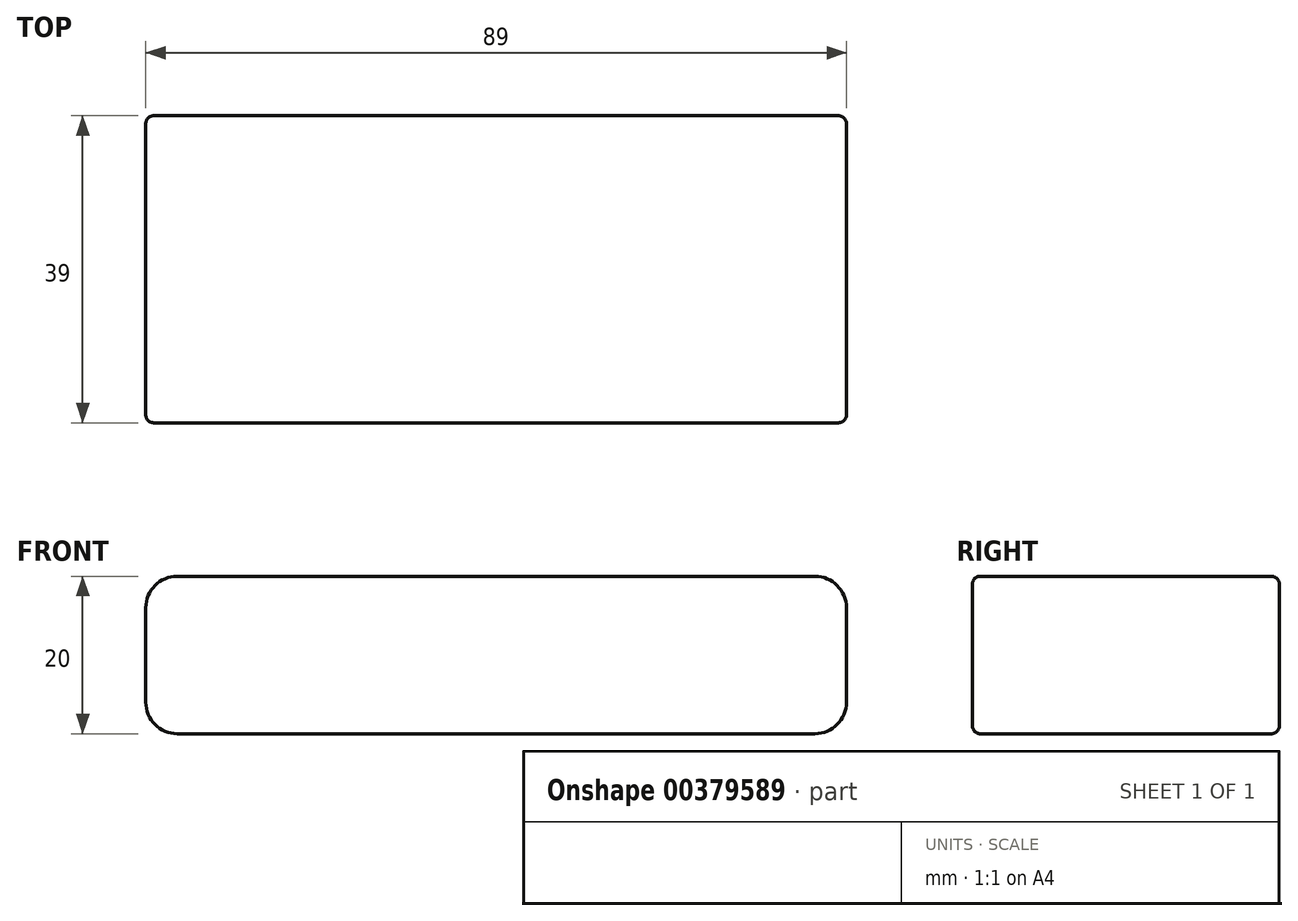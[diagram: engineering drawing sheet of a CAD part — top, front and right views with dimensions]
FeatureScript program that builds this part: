
annotation { "Feature Type Name" : "Feature", "Feature Type Description" : "" }
export const myFeature = defineFeature(function(context is Context, id is Id, definition is map)
    precondition{}
    {
        {
            var Q0;
            Q0=qCreatedBy(makeId("Top.planeOp"),FACE);
            var sketch = newSketch(context, id + "F0", { "sketchPlane" : qUnion([Q0])});
            skLineSegment(sketch, "E0.bottom", {"start": v(44.5, 19.5) * mm, "end": v(-44.5, 19.5) * mm});
            skLineSegment(sketch, "E0.top", {"start": v(44.5, -19.5) * mm, "end": v(-44.5, -19.5) * mm});
            skLineSegment(sketch, "E0.left", {"start": v(44.5, 19.5) * mm, "end": v(44.5, -19.5) * mm});
            skLineSegment(sketch, "E0.right", {"start": v(-44.5, 19.5) * mm, "end": v(-44.5, -19.5) * mm});
            skPoint(sketch, "E0.middle", {"position": v(0, 0) * mm});
            skSolve(sketch);
        }
        {
            var Q0;
            Q0=makeQuery(id+"F0.imprint","IMPRINT",FACE,{"disambiguationData":[TD([[makeQuery(id+"F0.imprint","IMPRINT",EDGE,{"derivedFrom":sQuery(id+"F0.wireOp",EDGE,"E0.bottom")}),1.0]])]});
            extrude(context, id + "F1", {"entities" : qUnion([Q0]), "depth" : 20 * mm});
        }
        {
            var Q0;
            Q0=makeQuery(id+"F1.opExtrude","CAP_EDGE",EDGE,{"disambiguationData":[OSD([sQuery(id+"F0.wireOp",EDGE,"E0.left")])],"isStart":false});
            var Q1;
            Q1=makeQuery(id+"F1.opExtrude","CAP_EDGE",EDGE,{"disambiguationData":[OSD([sQuery(id+"F0.wireOp",EDGE,"E0.left")])],"isStart":true});
            var Q2;
            Q2=makeQuery(id+"F1.opExtrude","CAP_EDGE",EDGE,{"disambiguationData":[OSD([sQuery(id+"F0.wireOp",EDGE,"E0.right")])],"isStart":false});
            var Q3;
            Q3=makeQuery(id+"F1.opExtrude","CAP_EDGE",EDGE,{"disambiguationData":[OSD([sQuery(id+"F0.wireOp",EDGE,"E0.right")])],"isStart":true});
            fillet(context, id + "F2", {"entities" : qUnion([Q0, Q1, Q2, Q3]), "radius" : 4 * mm, "tangentPropagation" : true, "allowEdgeOverflow" : false});
        }
        {
            var Q0;
            Q0=makeQuery(id+"F1.opExtrude","CAP_EDGE",EDGE,{"disambiguationData":[OSD([sQuery(id+"F0.wireOp",EDGE,"E0.top")])],"isStart":true});
            var Q1;
            Q1=makeQuery(id+"F1.opExtrude","CAP_EDGE",EDGE,{"disambiguationData":[OSD([sQuery(id+"F0.wireOp",EDGE,"E0.bottom")])],"isStart":true});
            fillet(context, id + "F3", {"entities" : qUnion([Q0, Q1]), "radius" : 1 * mm, "tangentPropagation" : true, "allowEdgeOverflow" : false});
        }
    });
